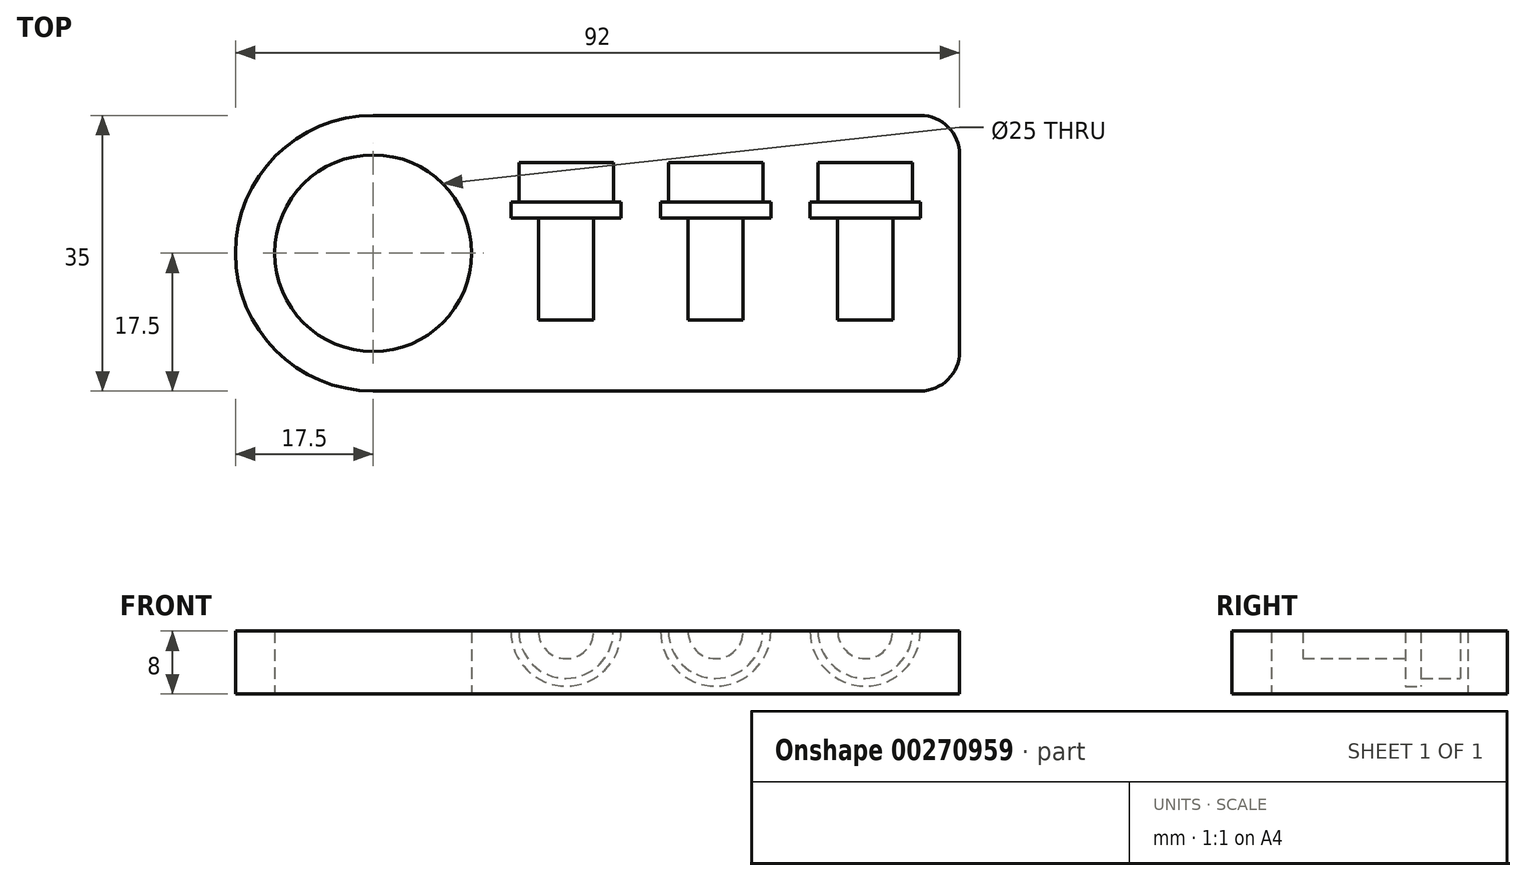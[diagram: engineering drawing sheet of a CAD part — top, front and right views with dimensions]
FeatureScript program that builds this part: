
annotation { "Feature Type Name" : "Feature", "Feature Type Description" : "" }
export const myFeature = defineFeature(function(context is Context, id is Id, definition is map)
    precondition{}
    {
        {
            var Q0;
            Q0=qCreatedBy(makeId("Top.planeOp"),FACE);
            var sketch = newSketch(context, id + "F0", { "sketchPlane" : qUnion([Q0])});
            skLineSegment(sketch, "E0.bottom", {"start": v(17.5, 0) * mm, "end": v(87, 0) * mm});
            skLineSegment(sketch, "E0.top", {"start": v(17.5, 35) * mm, "end": v(87, 35) * mm});
            skLineSegment(sketch, "E0.left", {"start": v(0, 17.5) * mm, "end": v(0, 17.5) * mm});
            skLineSegment(sketch, "E0.right", {"start": v(92, 5) * mm, "end": v(92, 30) * mm});
            skLineSegment(sketch, "E1.bottom", {"start": v(0, 0) * mm, "end": v(17.5, 0) * mm, "construction": true});
            skLineSegment(sketch, "E1.top", {"start": v(0, 17.5) * mm, "end": v(17.5, 17.5) * mm, "construction": true});
            skLineSegment(sketch, "E1.left", {"start": v(0, 0) * mm, "end": v(0, 17.5) * mm, "construction": true});
            skLineSegment(sketch, "E1.right", {"start": v(17.5, 0) * mm, "end": v(17.5, 17.5) * mm, "construction": true});
            skCircle(sketch, "E2", {"center": v(17.5, 17.5) * mm, "radius": 12.5 * mm});
            skPoint(sketch, "E3.visualSharp", {"position": v(0, 0) * mm});
            skArc(sketch, "E3.filletArc", {"start": v(0, 17.5) * mm, "mid": v(5.13, 5.13) * mm, "end": v(17.5, 0) * mm});
            skPoint(sketch, "E4.visualSharp", {"position": v(0, 35) * mm});
            skArc(sketch, "E4.filletArc", {"start": v(17.5, 35) * mm, "mid": v(5.13, 29.87) * mm, "end": v(0, 17.5) * mm});
            skPoint(sketch, "E5.visualSharp", {"position": v(92, 35) * mm});
            skArc(sketch, "E5.filletArc", {"start": v(92, 30) * mm, "mid": v(90.54, 33.54) * mm, "end": v(87, 35) * mm});
            skPoint(sketch, "E6.visualSharp", {"position": v(92, 0) * mm});
            skArc(sketch, "E6.filletArc", {"start": v(87, 0) * mm, "mid": v(90.54, 1.46) * mm, "end": v(92, 5) * mm});
            skSolve(sketch);
        }
        {
            var Q0;
            Q0=makeQuery(id+"F0.imprint","IMPRINT",FACE,{"disambiguationData":[TD([[makeQuery(id+"F0.imprint","IMPRINT",EDGE,{"derivedFrom":sQuery(id+"F0.wireOp",EDGE,"E0.bottom")}),1.0]])]});
            extrude(context, id + "F1", {"entities" : qUnion([Q0]), "depth" : 8 * mm});
        }
        {
            var Q0;
            Q0=makeQuery(id+"F1.opExtrude","CAP_FACE",FACE,{"disambiguationData":[OSD([sQuery(id+"F0.wireOp",EDGE,"E0.bottom"),sQuery(id+"F0.wireOp",EDGE,"E0.top"),sQuery(id+"F0.wireOp",EDGE,"E0.right"),sQuery(id+"F0.wireOp",EDGE,"E2"),sQuery(id+"F0.wireOp",EDGE,"E3.filletArc"),sQuery(id+"F0.wireOp",EDGE,"E4.filletArc"),sQuery(id+"F0.wireOp",EDGE,"E5.filletArc"),sQuery(id+"F0.wireOp",EDGE,"E6.filletArc")])],"isStart":false});
            var sketch = newSketch(context, id + "F2", { "sketchPlane" : qUnion([Q0])});
            skLineSegment(sketch, "E7.bottom", {"start": v(0, 0) * mm, "end": v(42, 0) * mm, "construction": true});
            skLineSegment(sketch, "E7.top", {"start": v(0, 9) * mm, "end": v(42, 9) * mm, "construction": true});
            skLineSegment(sketch, "E7.left", {"start": v(0, 0) * mm, "end": v(0, 9) * mm, "construction": true});
            skLineSegment(sketch, "E7.right", {"start": v(42, 0) * mm, "end": v(42, 9) * mm, "construction": true});
            skLineSegment(sketch, "E8", {"start": v(42, 9) * mm, "end": v(61, 9) * mm, "construction": true});
            skLineSegment(sketch, "E9", {"start": v(61, 9) * mm, "end": v(80, 9) * mm, "construction": true});
            skLineSegment(sketch, "E10.bottom", {"start": v(42, 9) * mm, "end": v(45.5, 9) * mm});
            skLineSegment(sketch, "E10.left", {"start": v(42, 9) * mm, "end": v(42, 22) * mm});
            skLineSegment(sketch, "E10.right", {"start": v(45.5, 9) * mm, "end": v(45.5, 22) * mm});
            skLineSegment(sketch, "E11.bottom", {"start": v(61, 9) * mm, "end": v(64.5, 9) * mm});
            skLineSegment(sketch, "E11.left", {"start": v(61, 9) * mm, "end": v(61, 22) * mm});
            skLineSegment(sketch, "E11.right", {"start": v(64.5, 9) * mm, "end": v(64.5, 22) * mm});
            skLineSegment(sketch, "E12.bottom", {"start": v(80, 9) * mm, "end": v(83.5, 9) * mm});
            skLineSegment(sketch, "E12.left", {"start": v(80, 9) * mm, "end": v(80, 22) * mm});
            skLineSegment(sketch, "E12.right", {"start": v(83.5, 9) * mm, "end": v(83.5, 22) * mm});
            skLineSegment(sketch, "E13.top", {"start": v(48, 24) * mm, "end": v(49, 24) * mm});
            skLineSegment(sketch, "E13.left", {"start": v(42, 22) * mm, "end": v(42, 24) * mm});
            skLineSegment(sketch, "E13.right", {"start": v(49, 22) * mm, "end": v(49, 24) * mm});
            skLineSegment(sketch, "E14.bottom", {"start": v(64.5, 22) * mm, "end": v(68, 22) * mm});
            skLineSegment(sketch, "E14.left", {"start": v(61, 22) * mm, "end": v(61, 24) * mm});
            skLineSegment(sketch, "E14.right", {"start": v(68, 22) * mm, "end": v(68, 24) * mm});
            skLineSegment(sketch, "E15.bottom", {"start": v(83.5, 22) * mm, "end": v(87, 22) * mm});
            skLineSegment(sketch, "E15.left", {"start": v(80, 22) * mm, "end": v(80, 24) * mm});
            skLineSegment(sketch, "E15.right", {"start": v(87, 22) * mm, "end": v(87, 24) * mm});
            skLineSegment(sketch, "E16.top", {"start": v(80, 29) * mm, "end": v(86, 29) * mm});
            skLineSegment(sketch, "E16.left", {"start": v(80, 24) * mm, "end": v(80, 29) * mm});
            skLineSegment(sketch, "E16.right", {"start": v(86, 24) * mm, "end": v(86, 29) * mm});
            skLineSegment(sketch, "E17.top", {"start": v(61, 29) * mm, "end": v(67, 29) * mm});
            skLineSegment(sketch, "E17.left", {"start": v(61, 24) * mm, "end": v(61, 29) * mm});
            skLineSegment(sketch, "E17.right", {"start": v(67, 24) * mm, "end": v(67, 29) * mm});
            skLineSegment(sketch, "E18.top", {"start": v(42, 29) * mm, "end": v(48, 29) * mm});
            skLineSegment(sketch, "E18.left", {"start": v(42, 24) * mm, "end": v(42, 29) * mm});
            skLineSegment(sketch, "E18.right", {"start": v(48, 24) * mm, "end": v(48, 29) * mm});
            skLineSegment(sketch, "E19", {"start": v(87, 24) * mm, "end": v(86, 24) * mm});
            skLineSegment(sketch, "E20", {"start": v(68, 24) * mm, "end": v(67, 24) * mm});
            skLineSegment(sketch, "E21", {"start": v(49, 22) * mm, "end": v(45.5, 22) * mm});
            skSolve(sketch);
        }
        {
            var Q0;
            Q0=makeQuery(id+"F2.imprint","IMPRINT",FACE,{"disambiguationData":[TD([[makeQuery(id+"F2.imprint","IMPRINT",EDGE,{"derivedFrom":sQuery(id+"F2.wireOp",EDGE,"E10.bottom")}),1.0]])]});
            var Q1;
            Q1=sQuery(id+"F2.wireOp",EDGE,"E10.left");
            revolve(context, id + "F3", {"operationType" : NewBodyOperationType.REMOVE, "entities" : qUnion([Q0]), "axis" : qUnion([Q1]), "revolveType" : RevolveType.FULL, "oppositeDirection" : true});
        }
        {
            var Q0;
            Q0=makeQuery(id+"F2.imprint","IMPRINT",FACE,{"disambiguationData":[TD([[makeQuery(id+"F2.imprint","IMPRINT",EDGE,{"derivedFrom":sQuery(id+"F2.wireOp",EDGE,"E11.bottom")}),1.0]])]});
            var Q1;
            Q1=sQuery(id+"F2.wireOp",EDGE,"E11.left");
            revolve(context, id + "F4", {"operationType" : NewBodyOperationType.REMOVE, "entities" : qUnion([Q0]), "axis" : qUnion([Q1]), "revolveType" : RevolveType.FULL, "oppositeDirection" : true});
        }
        {
            var Q0;
            Q0=makeQuery(id+"F2.imprint","IMPRINT",FACE,{"disambiguationData":[TD([[makeQuery(id+"F2.imprint","IMPRINT",EDGE,{"derivedFrom":sQuery(id+"F2.wireOp",EDGE,"E12.bottom")}),1.0]])]});
            var Q1;
            Q1=sQuery(id+"F2.wireOp",EDGE,"E12.left");
            revolve(context, id + "F5", {"operationType" : NewBodyOperationType.REMOVE, "entities" : qUnion([Q0]), "axis" : qUnion([Q1]), "revolveType" : RevolveType.FULL, "oppositeDirection" : true});
        }
    });
